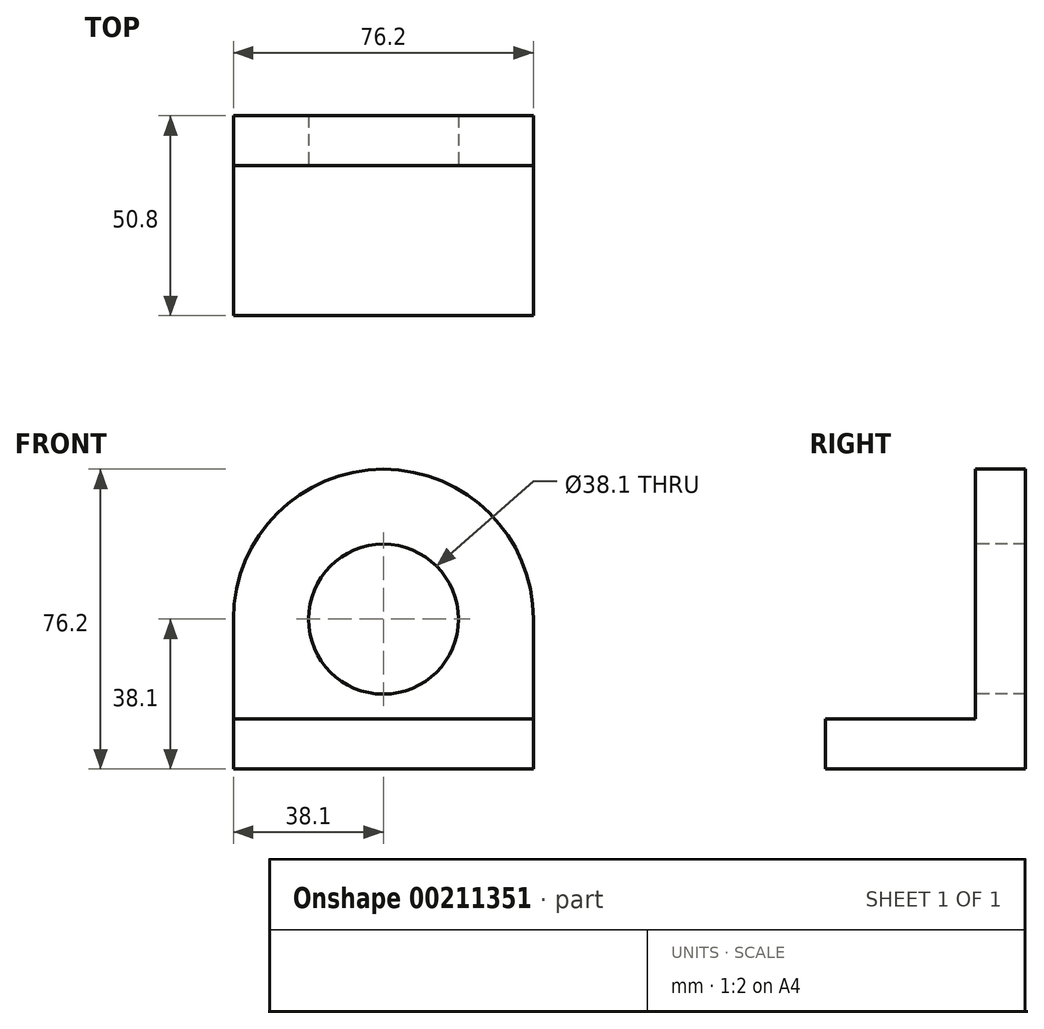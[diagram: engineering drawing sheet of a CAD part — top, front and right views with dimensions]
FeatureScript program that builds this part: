
annotation { "Feature Type Name" : "Feature", "Feature Type Description" : "" }
export const myFeature = defineFeature(function(context is Context, id is Id, definition is map)
    precondition{}
    {
        {
            var Q0;
            Q0=qCreatedBy(makeId("Top.planeOp"),FACE);
            var sketch = newSketch(context, id + "F0", { "sketchPlane" : qUnion([Q0])});
            skLineSegment(sketch, "E0", {"start": v(0, 0) * mm, "end": v(0, 50.8) * mm});
            skLineSegment(sketch, "E1", {"start": v(0, 50.8) * mm, "end": v(-76.2, 50.8) * mm});
            skLineSegment(sketch, "E2", {"start": v(-76.2, 50.8) * mm, "end": v(-76.2, 0) * mm});
            skLineSegment(sketch, "E3", {"start": v(-76.2, 0) * mm, "end": v(0, 0) * mm});
            skSolve(sketch);
        }
        {
            var Q0;
            Q0=makeQuery(id+"F0.imprint","IMPRINT",FACE,{"disambiguationData":[TD([[makeQuery(id+"F0.imprint","IMPRINT",EDGE,{"derivedFrom":sQuery(id+"F0.wireOp",EDGE,"E0")}),1.0]])]});
            extrude(context, id + "F1", {"entities" : qUnion([Q0]), "depth" : 12.7 * mm});
        }
        {
            var Q0;
            Q0=makeQuery(id+"F1.opExtrude","SWEPT_FACE",FACE,{"disambiguationData":[OSD([sQuery(id+"F0.wireOp",EDGE,"E0")])]});
            var sketch = newSketch(context, id + "F2", { "sketchPlane" : qUnion([Q0])});
            skLineSegment(sketch, "E4", {"start": v(50.8, 12.7) * mm, "end": v(50.8, 38.1) * mm});
            skLineSegment(sketch, "E5", {"start": v(50.8, 38.1) * mm, "end": v(38.1, 38.1) * mm});
            skLineSegment(sketch, "E6", {"start": v(38.1, 38.1) * mm, "end": v(38.1, 12.7) * mm});
            skSolve(sketch);
        }
        {
            var Q0;
            {var subQ0=sQuery(id+"F2.wireOp",EDGE,"E4");Q0=makeQuery(id+"F2.imprint","IMPRINT",FACE,{"disambiguationData":[TD([[makeQuery(id+"F2.imprint","IMPRINT",EDGE,{"derivedFrom":subQ0}),1.0]])]});}
            extrude(context, id + "F3", {"entities" : qUnion([Q0]), "operationType" : NewBodyOperationType.ADD, "oppositeDirection" : true, "depth" : 76.2 * mm});
        }
        {
            var Q0;
            Q0=makeQuery(id+"F3.opExtrude","SWEPT_FACE",FACE,{"disambiguationData":[OSD([sQuery(id+"F2.wireOp",EDGE,"E6")])]});
            var sketch = newSketch(context, id + "F4", { "sketchPlane" : qUnion([Q0])});
            skLineSegment(sketch, "E7", {"start": v(0, 38.1) * mm, "end": v(-38.1, 38.1) * mm});
            skCircle(sketch, "E8", {"center": v(-38.1, 38.1) * mm, "radius": 38.1 * mm});
            skCircle(sketch, "E9", {"center": v(-38.1, 38.1) * mm, "radius": 19.05 * mm});
            skSolve(sketch);
        }
        {
            var Q0;
            {var subQ1=sQuery(id+"F4.wireOp",EDGE,"E7");var subQ4=sQuery(id+"F4.wireOp",EDGE,"E9");var subQ5=makeQuery(id+"F4.imprint","INTERSECT",VERTEX,{"derivedFrom":[subQ1,subQ4]});Q0=makeQuery(id+"F4.imprint","IMPRINT",FACE,{"disambiguationData":[TD([[makeQuery(id+"F4.imprint","IMPRINT",EDGE,{"disambiguationData":[TD([[subQ5,-1.0]])],"derivedFrom":subQ1}),1.0]])]});}
            extrude(context, id + "F5", {"entities" : qUnion([Q0]), "operationType" : NewBodyOperationType.ADD, "oppositeDirection" : true, "depth" : 12.7 * mm});
        }
        {
            var Q0;
            {var subQ0=sQuery(id+"F2.wireOp",EDGE,"E6");Q0=makeQuery(id+"F5.boolean.opBoolean","MERGE",FACE,{"derivedFrom":[makeQuery(id+"F3.opExtrude","SWEPT_FACE",FACE,{"disambiguationData":[OSD([subQ0])]}),makeQuery(id+"F5.opExtrude","CAP_FACE",FACE,{"disambiguationData":[OSD([sQuery(id+"F2.wireOp",EDGE,"E5"),subQ0,sQuery(id+"F4.wireOp",EDGE,"E7"),sQuery(id+"F4.wireOp",EDGE,"E8"),sQuery(id+"F4.wireOp",EDGE,"E9")])],"isStart":true})]});}
            var sketch = newSketch(context, id + "F6", { "sketchPlane" : qUnion([Q0])});
            skCircle(sketch, "E10", {"center": v(-38.1, 38.1) * mm, "radius": 19.05 * mm});
            skSolve(sketch);
        }
        {
            var Q0;
            {var subQ1=makeQuery(id+"F3.opExtrude","SWEPT_EDGE",EDGE,{"disambiguationData":[OSD([sQuery(id+"F2.wireOp",EDGE,"E5"),sQuery(id+"F2.wireOp",EDGE,"E6")])]});Q0=makeQuery(id+"F6.imprint","IMPRINT",FACE,{"disambiguationData":[TD([[makeQuery(id+"F6.imprint","IMPRINT",EDGE,{"derivedFrom":subQ1}),-1.0]])]});}
            extrude(context, id + "F7", {"entities" : qUnion([Q0]), "operationType" : NewBodyOperationType.REMOVE, "oppositeDirection" : true, "depth" : 30.48 * mm});
        }
    });
